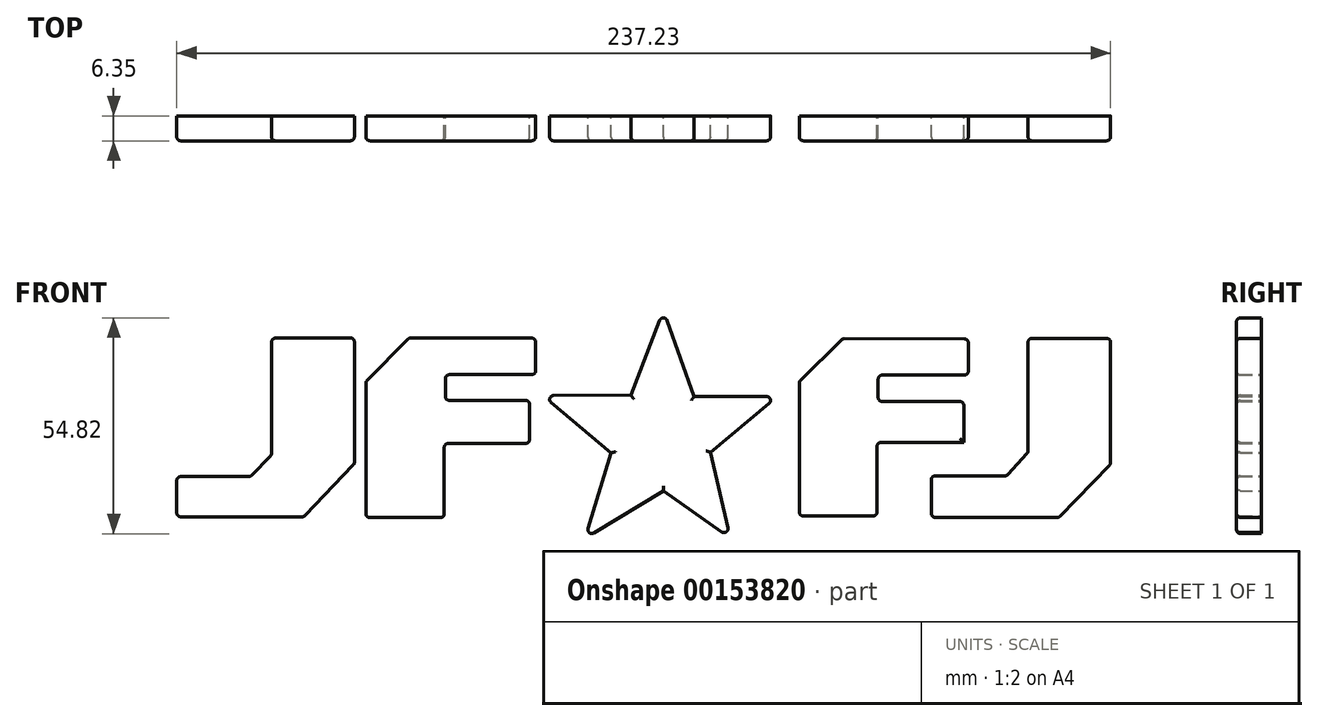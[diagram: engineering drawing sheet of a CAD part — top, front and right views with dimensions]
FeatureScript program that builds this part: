
annotation { "Feature Type Name" : "Feature", "Feature Type Description" : "" }
export const myFeature = defineFeature(function(context is Context, id is Id, definition is map)
    precondition{}
    {
        {
            var Q0;
            Q0=qCreatedBy(makeId("Front.planeOp"),FACE);
            var sketch = newSketch(context, id + "F0", { "sketchPlane" : qUnion([Q0])});
            skLineSegment(sketch, "E0", {"start": v(-99.58, 22.07) * mm, "end": v(-99.58, -7.56) * mm});
            skLineSegment(sketch, "E1", {"start": v(-99.58, -7.56) * mm, "end": v(-104.97, -13.1) * mm});
            skLineSegment(sketch, "E2", {"start": v(-104.97, -13.1) * mm, "end": v(-123.68, -13.1) * mm});
            skLineSegment(sketch, "E3", {"start": v(-123.68, -13.1) * mm, "end": v(-123.68, -23.33) * mm});
            skLineSegment(sketch, "E4", {"start": v(-123.68, -23.33) * mm, "end": v(-91.38, -23.33) * mm});
            skLineSegment(sketch, "E5", {"start": v(-91.38, -23.33) * mm, "end": v(-78.55, -9.88) * mm});
            skLineSegment(sketch, "E6", {"start": v(-78.55, -9.88) * mm, "end": v(-78.55, 22.12) * mm});
            skLineSegment(sketch, "E7", {"start": v(-78.55, 22.12) * mm, "end": v(-99.58, 22.07) * mm});
            skSolve(sketch);
        }
        {
            var Q0;
            Q0=makeQuery(id+"F0.imprint","IMPRINT",FACE,{"disambiguationData":[TD([[makeQuery(id+"F0.imprint","IMPRINT",EDGE,{"derivedFrom":sQuery(id+"F0.wireOp",EDGE,"E0")}),1.0]])]});
            extrude(context, id + "F1", {"entities" : qUnion([Q0]), "depth" : 6.35 * mm});
        }
        {
            var Q0;
            Q0=qCreatedBy(makeId("Front.planeOp"),FACE);
            var sketch = newSketch(context, id + "F2", { "sketchPlane" : qUnion([Q0])});
            skLineSegment(sketch, "E8", {"start": v(-64.57, 22.13) * mm, "end": v(-75.63, 11.01) * mm});
            skLineSegment(sketch, "E9", {"start": v(-75.63, 11.01) * mm, "end": v(-75.63, -23.55) * mm});
            skLineSegment(sketch, "E10", {"start": v(-75.63, -23.55) * mm, "end": v(-55.71, -23.55) * mm});
            skLineSegment(sketch, "E11", {"start": v(-55.71, -23.55) * mm, "end": v(-55.71, -4.7) * mm});
            skLineSegment(sketch, "E12", {"start": v(-55.71, -4.7) * mm, "end": v(-34.04, -4.7) * mm});
            skLineSegment(sketch, "E13", {"start": v(-34.04, -4.7) * mm, "end": v(-34.04, 6.24) * mm});
            skLineSegment(sketch, "E14", {"start": v(-34.04, 6.24) * mm, "end": v(-55.43, 6.24) * mm});
            skLineSegment(sketch, "E15", {"start": v(-55.43, 6.24) * mm, "end": v(-55.43, 12.77) * mm});
            skLineSegment(sketch, "E16", {"start": v(-55.43, 12.77) * mm, "end": v(-32.5, 12.77) * mm});
            skLineSegment(sketch, "E17", {"start": v(-32.5, 12.77) * mm, "end": v(-32.5, 22.08) * mm});
            skLineSegment(sketch, "E18", {"start": v(-32.5, 22.08) * mm, "end": v(-64.57, 22.13) * mm});
            skSolve(sketch);
        }
        {
            var Q0;
            Q0=makeQuery(id+"F2.imprint","IMPRINT",FACE,{"disambiguationData":[TD([[makeQuery(id+"F2.imprint","IMPRINT",EDGE,{"derivedFrom":sQuery(id+"F2.wireOp",EDGE,"E8")}),1.0]])]});
            extrude(context, id + "F3", {"entities" : qUnion([Q0]), "depth" : 6.35 * mm});
        }
        {
            var Q0;
            Q0=qCreatedBy(makeId("Front.planeOp"),FACE);
            var sketch = newSketch(context, id + "F4", { "sketchPlane" : qUnion([Q0])});
            skLineSegment(sketch, "E19", {"start": v(-8.29, 7.59) * mm, "end": v(0, 29.11) * mm});
            skLineSegment(sketch, "E20", {"start": v(0, 29.11) * mm, "end": v(7.78, 7.25) * mm});
            skLineSegment(sketch, "E21", {"start": v(7.78, 7.25) * mm, "end": v(28.96, 7.25) * mm});
            skLineSegment(sketch, "E22", {"start": v(28.96, 7.25) * mm, "end": v(11.9, -6.92) * mm});
            skLineSegment(sketch, "E23", {"start": v(11.9, -6.92) * mm, "end": v(16.95, -28.72) * mm});
            skLineSegment(sketch, "E24", {"start": v(16.95, -28.72) * mm, "end": v(0, -16.7) * mm});
            skLineSegment(sketch, "E25", {"start": v(0, -16.7) * mm, "end": v(-19.96, -28.85) * mm});
            skLineSegment(sketch, "E26", {"start": v(-19.96, -28.85) * mm, "end": v(-13.35, -7.12) * mm});
            skLineSegment(sketch, "E27", {"start": v(-13.35, -7.12) * mm, "end": v(-30.7, 7.45) * mm});
            skLineSegment(sketch, "E28", {"start": v(-30.7, 7.45) * mm, "end": v(-8.29, 7.59) * mm});
            skSolve(sketch);
        }
        {
            var Q0;
            Q0=makeQuery(id+"F4.imprint","IMPRINT",FACE,{"disambiguationData":[TD([[makeQuery(id+"F4.imprint","IMPRINT",EDGE,{"derivedFrom":sQuery(id+"F4.wireOp",EDGE,"E19")}),-1.0]])]});
            extrude(context, id + "F5", {"entities" : qUnion([Q0]), "depth" : 6.35 * mm});
        }
        {
            var Q0;
            Q0=makeQuery(id+"F5.opExtrude","SWEPT_EDGE",EDGE,{"disambiguationData":[OSD([sQuery(id+"F4.wireOp",EDGE,"E19"),sQuery(id+"F4.wireOp",EDGE,"E20")])]});
            var Q1;
            Q1=makeQuery(id+"F5.opExtrude","SWEPT_EDGE",EDGE,{"disambiguationData":[OSD([sQuery(id+"F4.wireOp",EDGE,"E27"),sQuery(id+"F4.wireOp",EDGE,"E28")])]});
            var Q2;
            Q2=makeQuery(id+"F5.opExtrude","SWEPT_EDGE",EDGE,{"disambiguationData":[OSD([sQuery(id+"F4.wireOp",EDGE,"E25"),sQuery(id+"F4.wireOp",EDGE,"E26")])]});
            var Q3;
            Q3=makeQuery(id+"F5.opExtrude","SWEPT_EDGE",EDGE,{"disambiguationData":[OSD([sQuery(id+"F4.wireOp",EDGE,"E23"),sQuery(id+"F4.wireOp",EDGE,"E24")])]});
            var Q4;
            Q4=makeQuery(id+"F5.opExtrude","SWEPT_EDGE",EDGE,{"disambiguationData":[OSD([sQuery(id+"F4.wireOp",EDGE,"E21"),sQuery(id+"F4.wireOp",EDGE,"E22")])]});
            fillet(context, id + "F6", {"entities" : qUnion([Q0, Q1, Q2, Q3, Q4]), "radius" : 1.02 * mm, "tangentPropagation" : true, "allowEdgeOverflow" : false});
        }
        {
            var Q0;
            Q0=makeQuery(id+"F3.opExtrude","SWEPT_EDGE",EDGE,{"disambiguationData":[OSD([sQuery(id+"F2.wireOp",EDGE,"E17"),sQuery(id+"F2.wireOp",EDGE,"E18")])]});
            var Q1;
            Q1=makeQuery(id+"F3.opExtrude","SWEPT_EDGE",EDGE,{"disambiguationData":[OSD([sQuery(id+"F2.wireOp",EDGE,"E16"),sQuery(id+"F2.wireOp",EDGE,"E17")])]});
            var Q2;
            Q2=makeQuery(id+"F3.opExtrude","SWEPT_EDGE",EDGE,{"disambiguationData":[OSD([sQuery(id+"F2.wireOp",EDGE,"E13"),sQuery(id+"F2.wireOp",EDGE,"E14")])]});
            var Q3;
            Q3=makeQuery(id+"F3.opExtrude","SWEPT_EDGE",EDGE,{"disambiguationData":[OSD([sQuery(id+"F2.wireOp",EDGE,"E12"),sQuery(id+"F2.wireOp",EDGE,"E13")])]});
            var Q4;
            Q4=makeQuery(id+"F3.opExtrude","SWEPT_EDGE",EDGE,{"disambiguationData":[OSD([sQuery(id+"F2.wireOp",EDGE,"E10"),sQuery(id+"F2.wireOp",EDGE,"E11")])]});
            var Q5;
            Q5=makeQuery(id+"F3.opExtrude","SWEPT_EDGE",EDGE,{"disambiguationData":[OSD([sQuery(id+"F2.wireOp",EDGE,"E14"),sQuery(id+"F2.wireOp",EDGE,"E15")])]});
            var Q6;
            Q6=makeQuery(id+"F3.opExtrude","SWEPT_EDGE",EDGE,{"disambiguationData":[OSD([sQuery(id+"F2.wireOp",EDGE,"E15"),sQuery(id+"F2.wireOp",EDGE,"E16")])]});
            var Q7;
            Q7=makeQuery(id+"F3.opExtrude","SWEPT_EDGE",EDGE,{"disambiguationData":[OSD([sQuery(id+"F2.wireOp",EDGE,"E9"),sQuery(id+"F2.wireOp",EDGE,"E10")])]});
            var Q8;
            Q8=makeQuery(id+"F3.opExtrude","SWEPT_EDGE",EDGE,{"disambiguationData":[OSD([sQuery(id+"F2.wireOp",EDGE,"E8"),sQuery(id+"F2.wireOp",EDGE,"E9")])]});
            var Q9;
            Q9=makeQuery(id+"F3.opExtrude","SWEPT_EDGE",EDGE,{"disambiguationData":[OSD([sQuery(id+"F2.wireOp",EDGE,"E8"),sQuery(id+"F2.wireOp",EDGE,"E18")])]});
            var Q10;
            Q10=makeQuery(id+"F3.opExtrude","SWEPT_EDGE",EDGE,{"disambiguationData":[OSD([sQuery(id+"F2.wireOp",EDGE,"E11"),sQuery(id+"F2.wireOp",EDGE,"E12")])]});
            fillet(context, id + "F7", {"entities" : qUnion([Q0, Q1, Q2, Q3, Q4, Q5, Q6, Q7, Q8, Q9, Q10]), "radius" : 1.02 * mm, "tangentPropagation" : true, "allowEdgeOverflow" : false});
        }
        {
            var Q0;
            Q0=makeQuery(id+"F1.opExtrude","SWEPT_EDGE",EDGE,{"disambiguationData":[OSD([sQuery(id+"F0.wireOp",EDGE,"E0"),sQuery(id+"F0.wireOp",EDGE,"E7")])]});
            var Q1;
            Q1=makeQuery(id+"F1.opExtrude","SWEPT_EDGE",EDGE,{"disambiguationData":[OSD([sQuery(id+"F0.wireOp",EDGE,"E0"),sQuery(id+"F0.wireOp",EDGE,"E1")])]});
            var Q2;
            Q2=makeQuery(id+"F1.opExtrude","SWEPT_EDGE",EDGE,{"disambiguationData":[OSD([sQuery(id+"F0.wireOp",EDGE,"E1"),sQuery(id+"F0.wireOp",EDGE,"E2")])]});
            var Q3;
            Q3=makeQuery(id+"F1.opExtrude","SWEPT_EDGE",EDGE,{"disambiguationData":[OSD([sQuery(id+"F0.wireOp",EDGE,"E2"),sQuery(id+"F0.wireOp",EDGE,"E3")])]});
            var Q4;
            Q4=makeQuery(id+"F1.opExtrude","SWEPT_EDGE",EDGE,{"disambiguationData":[OSD([sQuery(id+"F0.wireOp",EDGE,"E3"),sQuery(id+"F0.wireOp",EDGE,"E4")])]});
            var Q5;
            Q5=makeQuery(id+"F1.opExtrude","SWEPT_EDGE",EDGE,{"disambiguationData":[OSD([sQuery(id+"F0.wireOp",EDGE,"E6"),sQuery(id+"F0.wireOp",EDGE,"E7")])]});
            var Q6;
            Q6=makeQuery(id+"F1.opExtrude","SWEPT_EDGE",EDGE,{"disambiguationData":[OSD([sQuery(id+"F0.wireOp",EDGE,"E4"),sQuery(id+"F0.wireOp",EDGE,"E5")])]});
            var Q7;
            Q7=makeQuery(id+"F1.opExtrude","SWEPT_EDGE",EDGE,{"disambiguationData":[OSD([sQuery(id+"F0.wireOp",EDGE,"E5"),sQuery(id+"F0.wireOp",EDGE,"E6")])]});
            fillet(context, id + "F8", {"entities" : qUnion([Q0, Q1, Q2, Q3, Q4, Q5, Q6, Q7]), "radius" : 1.02 * mm, "tangentPropagation" : true, "allowEdgeOverflow" : false});
        }
        {
            var Q0;
            Q0=qCreatedBy(makeId("Front.planeOp"),FACE);
            var sketch = newSketch(context, id + "F9", { "sketchPlane" : qUnion([Q0])});
            skLineSegment(sketch, "E29", {"start": v(45.45, 21.92) * mm, "end": v(34.48, 11.04) * mm});
            skLineSegment(sketch, "E30", {"start": v(34.48, 11.04) * mm, "end": v(34.48, -23.13) * mm});
            skLineSegment(sketch, "E31", {"start": v(34.48, -23.13) * mm, "end": v(54.23, -23.13) * mm});
            skLineSegment(sketch, "E32", {"start": v(54.23, -23.13) * mm, "end": v(54.23, -4.42) * mm});
            skLineSegment(sketch, "E33", {"start": v(54.23, -4.42) * mm, "end": v(76.28, -4.42) * mm});
            skLineSegment(sketch, "E34", {"start": v(76.28, -4.42) * mm, "end": v(76.28, 5.98) * mm});
            skLineSegment(sketch, "E35", {"start": v(76.28, 5.98) * mm, "end": v(54.52, 5.98) * mm});
            skLineSegment(sketch, "E36", {"start": v(54.52, 5.98) * mm, "end": v(54.52, 12.66) * mm});
            skLineSegment(sketch, "E37", {"start": v(54.52, 12.66) * mm, "end": v(77.42, 12.66) * mm});
            skLineSegment(sketch, "E38", {"start": v(77.42, 12.66) * mm, "end": v(77.42, 21.87) * mm});
            skLineSegment(sketch, "E39", {"start": v(77.42, 21.87) * mm, "end": v(45.45, 21.92) * mm});
            skSolve(sketch);
        }
        {
            var Q0;
            Q0=makeQuery(id+"F9.imprint","IMPRINT",FACE,{"disambiguationData":[TD([[makeQuery(id+"F9.imprint","IMPRINT",EDGE,{"derivedFrom":sQuery(id+"F9.wireOp",EDGE,"E29")}),1.0]])]});
            extrude(context, id + "F10", {"entities" : qUnion([Q0]), "depth" : 6.35 * mm});
        }
        {
            var Q0;
            Q0=makeQuery(id+"F10.opExtrude","SWEPT_EDGE",EDGE,{"disambiguationData":[OSD([sQuery(id+"F9.wireOp",EDGE,"E29"),sQuery(id+"F9.wireOp",EDGE,"E39")])]});
            var Q1;
            Q1=makeQuery(id+"F10.opExtrude","SWEPT_EDGE",EDGE,{"disambiguationData":[OSD([sQuery(id+"F9.wireOp",EDGE,"E29"),sQuery(id+"F9.wireOp",EDGE,"E30")])]});
            var Q2;
            Q2=makeQuery(id+"F10.opExtrude","SWEPT_EDGE",EDGE,{"disambiguationData":[OSD([sQuery(id+"F9.wireOp",EDGE,"E34"),sQuery(id+"F9.wireOp",EDGE,"E35")])]});
            var Q3;
            Q3=makeQuery(id+"F10.opExtrude","SWEPT_EDGE",EDGE,{"disambiguationData":[OSD([sQuery(id+"F9.wireOp",EDGE,"E37"),sQuery(id+"F9.wireOp",EDGE,"E38")])]});
            var Q4;
            Q4=makeQuery(id+"F10.opExtrude","SWEPT_EDGE",EDGE,{"disambiguationData":[OSD([sQuery(id+"F9.wireOp",EDGE,"E38"),sQuery(id+"F9.wireOp",EDGE,"E39")])]});
            var Q5;
            Q5=makeQuery(id+"F10.opExtrude","SWEPT_EDGE",EDGE,{"disambiguationData":[OSD([sQuery(id+"F9.wireOp",EDGE,"E35"),sQuery(id+"F9.wireOp",EDGE,"E36")])]});
            var Q6;
            Q6=makeQuery(id+"F10.opExtrude","SWEPT_EDGE",EDGE,{"disambiguationData":[OSD([sQuery(id+"F9.wireOp",EDGE,"E31"),sQuery(id+"F9.wireOp",EDGE,"E32")])]});
            var Q7;
            Q7=makeQuery(id+"F10.opExtrude","SWEPT_EDGE",EDGE,{"disambiguationData":[OSD([sQuery(id+"F9.wireOp",EDGE,"E32"),sQuery(id+"F9.wireOp",EDGE,"E33")])]});
            var Q8;
            Q8=makeQuery(id+"F10.opExtrude","SWEPT_EDGE",EDGE,{"disambiguationData":[OSD([sQuery(id+"F9.wireOp",EDGE,"E36"),sQuery(id+"F9.wireOp",EDGE,"E37")])]});
            var Q9;
            Q9=makeQuery(id+"F10.opExtrude","SWEPT_EDGE",EDGE,{"disambiguationData":[OSD([sQuery(id+"F9.wireOp",EDGE,"E30"),sQuery(id+"F9.wireOp",EDGE,"E31")])]});
            fillet(context, id + "F11", {"entities" : qUnion([Q0, Q1, Q2, Q3, Q4, Q5, Q6, Q7, Q8, Q9]), "radius" : 1.02 * mm, "tangentPropagation" : true, "allowEdgeOverflow" : false});
        }
        {
            var Q0;
            Q0=qCreatedBy(makeId("Front.planeOp"),FACE);
            var sketch = newSketch(context, id + "F12", { "sketchPlane" : qUnion([Q0])});
            skLineSegment(sketch, "E40", {"start": v(92.6, 22.03) * mm, "end": v(92.6, -6.98) * mm});
            skLineSegment(sketch, "E41", {"start": v(92.6, -6.98) * mm, "end": v(87.21, -12.9) * mm});
            skLineSegment(sketch, "E42", {"start": v(87.21, -12.9) * mm, "end": v(68.03, -12.9) * mm});
            skLineSegment(sketch, "E43", {"start": v(68.03, -12.9) * mm, "end": v(68.03, -23.5) * mm});
            skLineSegment(sketch, "E44", {"start": v(68.03, -23.5) * mm, "end": v(100.43, -23.5) * mm});
            skLineSegment(sketch, "E45", {"start": v(100.43, -23.5) * mm, "end": v(113.55, -9.94) * mm});
            skLineSegment(sketch, "E46", {"start": v(113.55, -9.94) * mm, "end": v(113.55, 22.03) * mm});
            skLineSegment(sketch, "E47", {"start": v(113.55, 22.03) * mm, "end": v(92.6, 22.03) * mm});
            skSolve(sketch);
        }
        {
            var Q0;
            Q0=makeQuery(id+"F12.imprint","IMPRINT",FACE,{"disambiguationData":[TD([[makeQuery(id+"F12.imprint","IMPRINT",EDGE,{"derivedFrom":sQuery(id+"F12.wireOp",EDGE,"E40")}),1.0]])]});
            extrude(context, id + "F13", {"entities" : qUnion([Q0]), "depth" : 6.35 * mm});
        }
        {
            var Q0;
            Q0=makeQuery(id+"F13.opExtrude","SWEPT_EDGE",EDGE,{"disambiguationData":[OSD([sQuery(id+"F12.wireOp",EDGE,"E42"),sQuery(id+"F12.wireOp",EDGE,"E43")])]});
            var Q1;
            Q1=makeQuery(id+"F13.opExtrude","SWEPT_EDGE",EDGE,{"disambiguationData":[OSD([sQuery(id+"F12.wireOp",EDGE,"E41"),sQuery(id+"F12.wireOp",EDGE,"E42")])]});
            var Q2;
            Q2=makeQuery(id+"F13.opExtrude","SWEPT_EDGE",EDGE,{"disambiguationData":[OSD([sQuery(id+"F12.wireOp",EDGE,"E40"),sQuery(id+"F12.wireOp",EDGE,"E41")])]});
            var Q3;
            Q3=makeQuery(id+"F13.opExtrude","SWEPT_EDGE",EDGE,{"disambiguationData":[OSD([sQuery(id+"F12.wireOp",EDGE,"E40"),sQuery(id+"F12.wireOp",EDGE,"E47")])]});
            var Q4;
            Q4=makeQuery(id+"F13.opExtrude","SWEPT_EDGE",EDGE,{"disambiguationData":[OSD([sQuery(id+"F12.wireOp",EDGE,"E46"),sQuery(id+"F12.wireOp",EDGE,"E47")])]});
            var Q5;
            Q5=makeQuery(id+"F13.opExtrude","SWEPT_EDGE",EDGE,{"disambiguationData":[OSD([sQuery(id+"F12.wireOp",EDGE,"E45"),sQuery(id+"F12.wireOp",EDGE,"E46")])]});
            var Q6;
            Q6=makeQuery(id+"F13.opExtrude","SWEPT_EDGE",EDGE,{"disambiguationData":[OSD([sQuery(id+"F12.wireOp",EDGE,"E44"),sQuery(id+"F12.wireOp",EDGE,"E45")])]});
            var Q7;
            Q7=makeQuery(id+"F13.opExtrude","SWEPT_EDGE",EDGE,{"disambiguationData":[OSD([sQuery(id+"F12.wireOp",EDGE,"E43"),sQuery(id+"F12.wireOp",EDGE,"E44")])]});
            fillet(context, id + "F14", {"entities" : qUnion([Q0, Q1, Q2, Q3, Q4, Q5, Q6, Q7]), "radius" : 1.02 * mm, "tangentPropagation" : true, "allowEdgeOverflow" : false});
        }
        {
            var Q0;
            Q0=makeQuery(id+"F1.opExtrude","CAP_FACE",FACE,{"disambiguationData":[OSD([sQuery(id+"F0.wireOp",EDGE,"E0"),sQuery(id+"F0.wireOp",EDGE,"E1"),sQuery(id+"F0.wireOp",EDGE,"E2"),sQuery(id+"F0.wireOp",EDGE,"E3"),sQuery(id+"F0.wireOp",EDGE,"E4"),sQuery(id+"F0.wireOp",EDGE,"E5"),sQuery(id+"F0.wireOp",EDGE,"E6"),sQuery(id+"F0.wireOp",EDGE,"E7")])],"isStart":false});
            fillet(context, id + "F15", {"entities" : qUnion([Q0]), "radius" : 1.02 * mm, "tangentPropagation" : true, "allowEdgeOverflow" : false});
        }
        {
            var Q0;
            Q0=makeQuery(id+"F3.opExtrude","CAP_FACE",FACE,{"disambiguationData":[OSD([sQuery(id+"F2.wireOp",EDGE,"E8"),sQuery(id+"F2.wireOp",EDGE,"E9"),sQuery(id+"F2.wireOp",EDGE,"E10"),sQuery(id+"F2.wireOp",EDGE,"E11"),sQuery(id+"F2.wireOp",EDGE,"E12"),sQuery(id+"F2.wireOp",EDGE,"E13"),sQuery(id+"F2.wireOp",EDGE,"E14"),sQuery(id+"F2.wireOp",EDGE,"E15"),sQuery(id+"F2.wireOp",EDGE,"E16"),sQuery(id+"F2.wireOp",EDGE,"E17"),sQuery(id+"F2.wireOp",EDGE,"E18")])],"isStart":false});
            fillet(context, id + "F16", {"entities" : qUnion([Q0]), "radius" : 1.02 * mm, "tangentPropagation" : true, "allowEdgeOverflow" : false});
        }
        {
            var Q0;
            Q0=makeQuery(id+"F5.opExtrude","CAP_FACE",FACE,{"disambiguationData":[OSD([sQuery(id+"F4.wireOp",EDGE,"E19"),sQuery(id+"F4.wireOp",EDGE,"E20"),sQuery(id+"F4.wireOp",EDGE,"E21"),sQuery(id+"F4.wireOp",EDGE,"E22"),sQuery(id+"F4.wireOp",EDGE,"E23"),sQuery(id+"F4.wireOp",EDGE,"E24"),sQuery(id+"F4.wireOp",EDGE,"E25"),sQuery(id+"F4.wireOp",EDGE,"E26"),sQuery(id+"F4.wireOp",EDGE,"E27"),sQuery(id+"F4.wireOp",EDGE,"E28")])],"isStart":false});
            fillet(context, id + "F17", {"entities" : qUnion([Q0]), "radius" : 1.02 * mm, "tangentPropagation" : true, "allowEdgeOverflow" : false});
        }
        {
            var Q0;
            Q0=makeQuery(id+"F10.opExtrude","CAP_FACE",FACE,{"disambiguationData":[OSD([sQuery(id+"F9.wireOp",EDGE,"E29"),sQuery(id+"F9.wireOp",EDGE,"E30"),sQuery(id+"F9.wireOp",EDGE,"E31"),sQuery(id+"F9.wireOp",EDGE,"E32"),sQuery(id+"F9.wireOp",EDGE,"E33"),sQuery(id+"F9.wireOp",EDGE,"E34"),sQuery(id+"F9.wireOp",EDGE,"E35"),sQuery(id+"F9.wireOp",EDGE,"E36"),sQuery(id+"F9.wireOp",EDGE,"E37"),sQuery(id+"F9.wireOp",EDGE,"E38"),sQuery(id+"F9.wireOp",EDGE,"E39")])],"isStart":false});
            fillet(context, id + "F18", {"entities" : qUnion([Q0]), "radius" : 1.02 * mm, "tangentPropagation" : true, "allowEdgeOverflow" : false});
        }
        {
            var Q0;
            Q0=makeQuery(id+"F13.opExtrude","CAP_FACE",FACE,{"disambiguationData":[OSD([sQuery(id+"F12.wireOp",EDGE,"E40"),sQuery(id+"F12.wireOp",EDGE,"E41"),sQuery(id+"F12.wireOp",EDGE,"E42"),sQuery(id+"F12.wireOp",EDGE,"E43"),sQuery(id+"F12.wireOp",EDGE,"E44"),sQuery(id+"F12.wireOp",EDGE,"E45"),sQuery(id+"F12.wireOp",EDGE,"E46"),sQuery(id+"F12.wireOp",EDGE,"E47")])],"isStart":false});
            fillet(context, id + "F19", {"entities" : qUnion([Q0]), "radius" : 1.02 * mm, "tangentPropagation" : true, "allowEdgeOverflow" : false});
        }
    });
